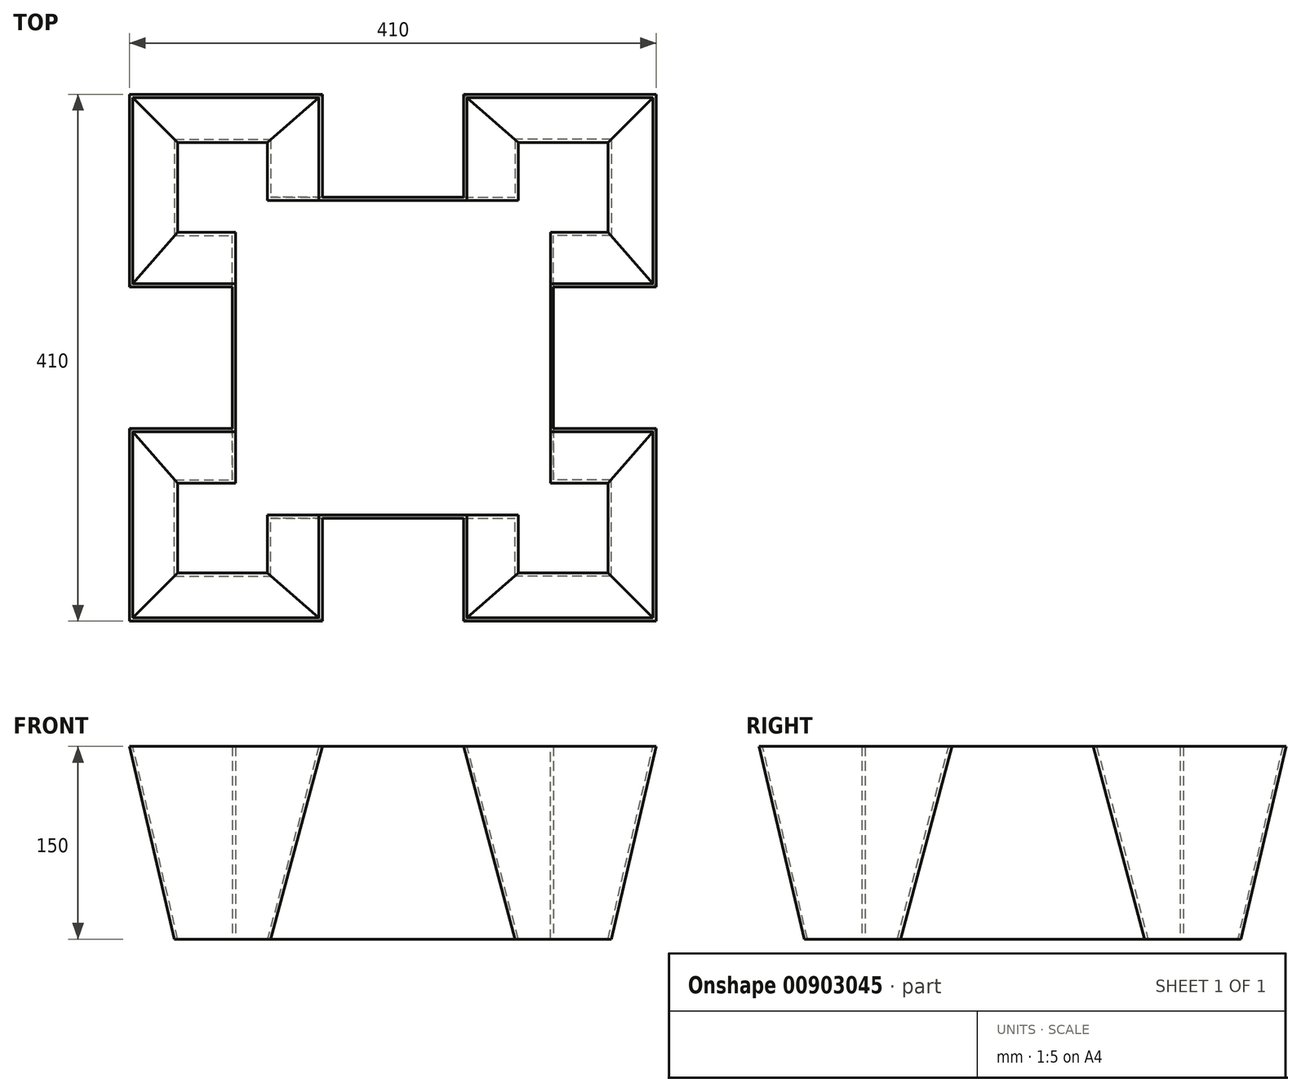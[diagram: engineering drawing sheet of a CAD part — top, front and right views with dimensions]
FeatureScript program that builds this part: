
annotation { "Feature Type Name" : "Feature", "Feature Type Description" : "" }
export const myFeature = defineFeature(function(context is Context, id is Id, definition is map)
    precondition{}
    {
        {
            var Q0;
            Q0=qCreatedBy(makeId("Top.planeOp"),FACE);
            var sketch = newSketch(context, id + "F0", { "sketchPlane" : qUnion([Q0])});
            skLineSegment(sketch, "E0.bottom", {"start": v(-55, 125) * mm, "end": v(55, 125) * mm});
            skLineSegment(sketch, "E0.top", {"start": v(-55, -125) * mm, "end": v(55, -125) * mm});
            skLineSegment(sketch, "E0.left", {"start": v(-125, 55) * mm, "end": v(-125, -55) * mm});
            skLineSegment(sketch, "E0.right", {"start": v(125, 55) * mm, "end": v(125, -55) * mm});
            skPoint(sketch, "E1", {"position": v(-130, 130) * mm});
            skLineSegment(sketch, "E2.bottom", {"start": v(-205, 205) * mm, "end": v(-55, 205) * mm});
            skLineSegment(sketch, "E2.top", {"start": v(-205, 55) * mm, "end": v(-125, 55) * mm});
            skLineSegment(sketch, "E2.left", {"start": v(-205, 205) * mm, "end": v(-205, 55) * mm});
            skLineSegment(sketch, "E2.right", {"start": v(-55, 205) * mm, "end": v(-55, 125) * mm});
            skLineSegment(sketch, "E3.1.0", {"start": v(-205, -55) * mm, "end": v(-125, -55) * mm});
            skLineSegment(sketch, "E3.1.1", {"start": v(-205, -205) * mm, "end": v(-205, -55) * mm});
            skLineSegment(sketch, "E3.1.2", {"start": v(-205, -205) * mm, "end": v(-55, -205) * mm});
            skLineSegment(sketch, "E3.1.3", {"start": v(-55, -205) * mm, "end": v(-55, -125) * mm});
            skLineSegment(sketch, "E3.2.0", {"start": v(55, -205) * mm, "end": v(55, -125) * mm});
            skLineSegment(sketch, "E3.2.1", {"start": v(205, -205) * mm, "end": v(55, -205) * mm});
            skLineSegment(sketch, "E3.2.2", {"start": v(205, -205) * mm, "end": v(205, -55) * mm});
            skLineSegment(sketch, "E3.2.3", {"start": v(205, -55) * mm, "end": v(125, -55) * mm});
            skLineSegment(sketch, "E3.3.0", {"start": v(205, 55) * mm, "end": v(125, 55) * mm});
            skLineSegment(sketch, "E3.3.1", {"start": v(205, 205) * mm, "end": v(205, 55) * mm});
            skLineSegment(sketch, "E3.3.2", {"start": v(205, 205) * mm, "end": v(55, 205) * mm});
            skLineSegment(sketch, "E3.3.3", {"start": v(55, 205) * mm, "end": v(55, 125) * mm});
            skPoint(sketch, "E3.center", {"position": v(0, 0) * mm});
            skPoint(sketch, "E4.orphan", {"position": v(-55, 55) * mm});
            skPoint(sketch, "E5.orphan", {"position": v(55, 55) * mm});
            skPoint(sketch, "E6.orphan", {"position": v(55, -55) * mm});
            skPoint(sketch, "E7.orphan", {"position": v(-55, -55) * mm});
            skSolve(sketch);
        }
        {
            var Q0;
            Q0=qCreatedBy(makeId("Top.planeOp"),FACE);
            cPlane(context, id + "F1", {"entities" : qUnion([Q0]), "cplaneType" : CPlaneType.OFFSET, "offset" : 150 * mm, "oppositeDirection" : true, "width" : 150 * mm, "height" : 150 * mm});
        }
        {
            var Q0;
            Q0=qCreatedBy(id+"F1.planeOp",FACE);
            var sketch = newSketch(context, id + "F2", { "sketchPlane" : qUnion([Q0])});
            skLineSegment(sketch, "E8.bottom", {"start": v(-95, -125) * mm, "end": v(95, -125) * mm});
            skLineSegment(sketch, "E8.top", {"start": v(-95, 125) * mm, "end": v(95, 125) * mm});
            skLineSegment(sketch, "E8.left", {"start": v(-125, -95) * mm, "end": v(-125, 95) * mm});
            skLineSegment(sketch, "E8.right", {"start": v(125, -95) * mm, "end": v(125, 95) * mm});
            skLineSegment(sketch, "E9.bottom", {"start": v(-170, 170) * mm, "end": v(-95, 170) * mm});
            skLineSegment(sketch, "E9.top", {"start": v(-170, 95) * mm, "end": v(-125, 95) * mm});
            skLineSegment(sketch, "E9.left", {"start": v(-170, 170) * mm, "end": v(-170, 95) * mm});
            skLineSegment(sketch, "E9.right", {"start": v(-95, 170) * mm, "end": v(-95, 125) * mm});
            skLineSegment(sketch, "E10.1.0", {"start": v(-170, -95) * mm, "end": v(-125, -95) * mm});
            skLineSegment(sketch, "E10.1.1", {"start": v(-95, -170) * mm, "end": v(-95, -125) * mm});
            skLineSegment(sketch, "E10.1.2", {"start": v(-170, -170) * mm, "end": v(-95, -170) * mm});
            skLineSegment(sketch, "E10.1.3", {"start": v(-170, -170) * mm, "end": v(-170, -95) * mm});
            skLineSegment(sketch, "E10.2.0", {"start": v(95, -170) * mm, "end": v(95, -125) * mm});
            skLineSegment(sketch, "E10.2.1", {"start": v(170, -95) * mm, "end": v(125, -95) * mm});
            skLineSegment(sketch, "E10.2.2", {"start": v(170, -170) * mm, "end": v(170, -95) * mm});
            skLineSegment(sketch, "E10.2.3", {"start": v(170, -170) * mm, "end": v(95, -170) * mm});
            skLineSegment(sketch, "E10.3.0", {"start": v(170, 95) * mm, "end": v(125, 95) * mm});
            skLineSegment(sketch, "E10.3.1", {"start": v(95, 170) * mm, "end": v(95, 125) * mm});
            skLineSegment(sketch, "E10.3.2", {"start": v(170, 170) * mm, "end": v(95, 170) * mm});
            skLineSegment(sketch, "E10.3.3", {"start": v(170, 170) * mm, "end": v(170, 95) * mm});
            skPoint(sketch, "E10.center", {"position": v(0, 0) * mm});
            skPoint(sketch, "E11.orphan", {"position": v(-95, 95) * mm});
            skPoint(sketch, "E12.orphan", {"position": v(95, 95) * mm});
            skPoint(sketch, "E13.orphan", {"position": v(95, -95) * mm});
            skPoint(sketch, "E14.orphan", {"position": v(-95, -95) * mm});
            skSolve(sketch);
        }
        {
            var Q0;
            Q0=makeQuery(id+"F0.imprint","IMPRINT",FACE,{"disambiguationData":[TD([[makeQuery(id+"F0.imprint","IMPRINT",EDGE,{"derivedFrom":sQuery(id+"F0.wireOp",EDGE,"E0.bottom")}),-1.0]])]});
            var Q1;
            Q1=makeQuery(id+"F2.imprint","IMPRINT",FACE,{"disambiguationData":[TD([[makeQuery(id+"F2.imprint","IMPRINT",EDGE,{"derivedFrom":sQuery(id+"F2.wireOp",EDGE,"E8.bottom")}),1.0]])]});
            loft(context, id + "F3", {"sheetProfilesArray" : [{ "sheetProfileEntities" : qUnion([Q0]) }, { "sheetProfileEntities" : qUnion([Q1]) }]});
        }
        {
            var Q0;
            Q0=makeQuery(id+"F3.opLoft","CAP_FACE",FACE,{"disambiguationData":[OSD([makeQuery(id+"F0.imprint","IMPRINT",FACE,{"disambiguationData":[TD([[makeQuery(id+"F0.imprint","IMPRINT",EDGE,{"derivedFrom":sQuery(id+"F0.wireOp",EDGE,"E0.bottom")}),-1.0]])]})])],"isStart":true});
            var Q1;
            Q1=makeQuery(id+"F3.opLoft","CAP_FACE",FACE,{"disambiguationData":[OSD([makeQuery(id+"F2.imprint","IMPRINT",FACE,{"disambiguationData":[TD([[makeQuery(id+"F2.imprint","IMPRINT",EDGE,{"derivedFrom":sQuery(id+"F2.wireOp",EDGE,"E8.bottom")}),1.0]])]})])],"isStart":true});
            shell(context, id + "F4", {"entities" : qUnion([Q0, Q1]), "thickness" : 2.5 * mm});
        }
    });
